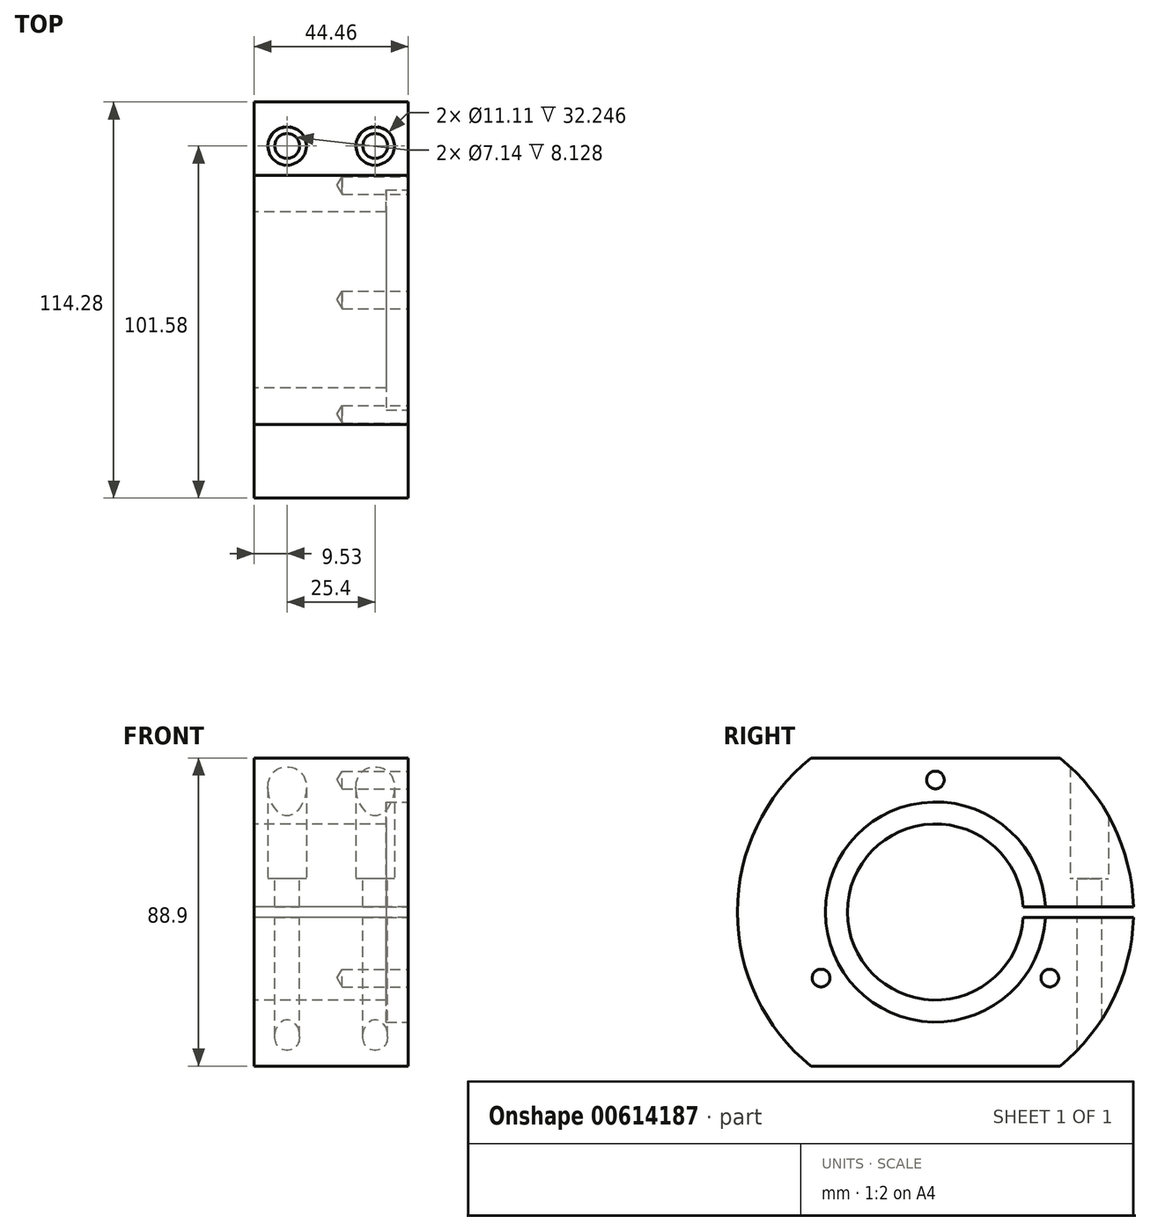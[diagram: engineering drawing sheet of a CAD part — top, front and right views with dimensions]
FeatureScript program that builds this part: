
annotation { "Feature Type Name" : "Feature", "Feature Type Description" : "" }
export const myFeature = defineFeature(function(context is Context, id is Id, definition is map)
    precondition{}
    {
        {
            var Q0;
            Q0=qCreatedBy(makeId("Right.planeOp"),FACE);
            var sketch = newSketch(context, id + "F0", { "sketchPlane" : qUnion([Q0])});
            skCircle(sketch, "E0", {"center": v(0, 0) * mm, "radius": 25.4 * mm});
            skArc(sketch, "E1", {"start": v(-35.92, 44.45) * mm, "mid": v(-57.15, 0) * mm, "end": v(-35.92, -44.45) * mm});
            skLineSegment(sketch, "E2", {"start": v(-95, 0) * mm, "end": v(101.51, 0) * mm, "construction": true});
            skLineSegment(sketch, "E3.0", {"start": v(-35.92, 44.45) * mm, "end": v(35.92, 44.45) * mm});
            skLineSegment(sketch, "E4.MirrorCS", {"start": v(-35.92, -44.45) * mm, "end": v(35.92, -44.45) * mm});
            skArc(sketch, "E5.trimOffspring", {"start": v(35.92, -44.45) * mm, "mid": v(57.15, 0) * mm, "end": v(35.92, 44.45) * mm});
            skPoint(sketch, "E6.orphan", {"position": v(101.51, -44.45) * mm});
            skPoint(sketch, "E7.orphan", {"position": v(-95, -44.45) * mm});
            skPoint(sketch, "E8.orphan", {"position": v(-95, 44.45) * mm});
            skPoint(sketch, "E9.orphan", {"position": v(101.51, 44.45) * mm});
            skSolve(sketch);
        }
        {
            var Q0;
            Q0 = qSketchRegion(id + "F0", true);
            extrude(context, id + "F1", {"entities" : qUnion([Q0]), "endBound" : BoundingType.SYMMETRIC, "depth" : 44.45 * mm, "offsetDistance" : 25.4 * mm});
        }
        {
            var Q0;
            Q0=makeQuery(id+"F1.opExtrude","CAP_FACE",FACE,{"disambiguationData":[OSD([sQuery(id+"F0.wireOp",EDGE,"E0"),sQuery(id+"F0.wireOp",EDGE,"E1"),sQuery(id+"F0.wireOp",EDGE,"E3.0"),sQuery(id+"F0.wireOp",EDGE,"E4.MirrorCS"),sQuery(id+"F0.wireOp",EDGE,"E5.trimOffspring")])],"isStart":false});
            var sketch = newSketch(context, id + "F2", { "sketchPlane" : qUnion([Q0])});
            skCircle(sketch, "E10", {"center": v(0, 0) * mm, "radius": 31.75 * mm});
            skSolve(sketch);
        }
        {
            var Q0;
            Q0 = qSketchRegion(id + "F2", true);
            extrude(context, id + "F3", {"entities" : qUnion([Q0]), "operationType" : NewBodyOperationType.REMOVE, "oppositeDirection" : true, "depth" : 6.35 * mm, "offsetDistance" : 25.4 * mm});
        }
        {
            var Q0;
            Q0=makeQuery(id+"F1.opExtrude","CAP_FACE",FACE,{"disambiguationData":[OSD([sQuery(id+"F0.wireOp",EDGE,"E0"),sQuery(id+"F0.wireOp",EDGE,"E1"),sQuery(id+"F0.wireOp",EDGE,"E3.0"),sQuery(id+"F0.wireOp",EDGE,"E4.MirrorCS"),sQuery(id+"F0.wireOp",EDGE,"E5.trimOffspring")])],"isStart":false});
            var sketch = newSketch(context, id + "F4", { "sketchPlane" : qUnion([Q0])});
            skLineSegment(sketch, "E11", {"start": v(5.07, 0) * mm, "end": v(74.02, 0) * mm});
            skLineSegment(sketch, "E12.0", {"start": v(5.07, -1.52) * mm, "end": v(74.02, -1.52) * mm});
            skLineSegment(sketch, "E13.0", {"start": v(5.07, 1.52) * mm, "end": v(74.02, 1.52) * mm});
            skLineSegment(sketch, "E14", {"start": v(5.07, 1.52) * mm, "end": v(5.07, -1.52) * mm});
            skLineSegment(sketch, "E15", {"start": v(74.02, 1.52) * mm, "end": v(74.02, -1.52) * mm});
            skSolve(sketch);
        }
        {
            var Q0;
            Q0 = qSketchRegion(id + "F4", true);
            extrude(context, id + "F5", {"entities" : qUnion([Q0]), "operationType" : NewBodyOperationType.REMOVE, "endBound" : BoundingType.THROUGH_ALL, "oppositeDirection" : true, "depth" : 25.4 * mm, "offsetDistance" : 25.4 * mm});
        }
        {
            var Q0;
            Q0=qCreatedBy(makeId("Top.planeOp"),FACE);
            cPlane(context, id + "F6", {"entities" : qUnion([Q0]), "cplaneType" : CPlaneType.OFFSET, "offset" : 9.65 * mm, "width" : 152.4 * mm, "height" : 152.4 * mm});
        }
        {
            var Q0;
            Q0=qCreatedBy(id+"F6.planeOp",FACE);
            var sketch = newSketch(context, id + "F7", { "sketchPlane" : qUnion([Q0])});
            skLineSegment(sketch, "E16.0", {"start": v(-22.23, 57.13) * mm, "end": v(22.23, 57.13) * mm, "construction": true});
            skLineSegment(sketch, "E17.0", {"start": v(-22.23, 25.35) * mm, "end": v(22.23, 25.35) * mm, "construction": true});
            skPoint(sketch, "E18.orphan", {"position": v(15.88, 25.35) * mm});
            skLineSegment(sketch, "E19.0", {"start": v(22.23, -35.92) * mm, "end": v(22.23, 35.92) * mm, "construction": true});
            skLineSegment(sketch, "E20.0", {"start": v(-22.23, -35.92) * mm, "end": v(-22.23, 35.92) * mm, "construction": true});
            skLineSegment(sketch, "E21", {"start": v(0, 25.35) * mm, "end": v(0, 57.13) * mm, "construction": true});
            skLineSegment(sketch, "E22.0", {"start": v(12.7, 25.35) * mm, "end": v(12.7, 57.13) * mm, "construction": true});
            skCircle(sketch, "E23", {"center": v(12.7, 44.43) * mm, "radius": 5.56 * mm});
            skCircle(sketch, "E24.MirrorC", {"center": v(-12.7, 44.43) * mm, "radius": 5.56 * mm});
            skSolve(sketch);
        }
        {
            var Q0;
            Q0 = qSketchRegion(id + "F7", true);
            extrude(context, id + "F8", {"entities" : qUnion([Q0]), "operationType" : NewBodyOperationType.REMOVE, "depth" : 50.8 * mm, "offsetDistance" : 25.4 * mm});
        }
        {
            var Q0;
            Q0=makeQuery(id+"F8.boolean.opBoolean","COPY",FACE,{"derivedFrom":makeQuery(id+"F8.opExtrude","CAP_FACE",FACE,{"disambiguationData":[OSD([sQuery(id+"F7.wireOp",EDGE,"E23")])],"isStart":true})});
            var sketch = newSketch(context, id + "F9", { "sketchPlane" : qUnion([Q0])});
            skLineSegment(sketch, "E25.0", {"start": v(0, 25.35) * mm, "end": v(0, 57.13) * mm, "construction": true});
            skPoint(sketch, "E26", {"position": v(12.7, 44.43) * mm});
            skPoint(sketch, "E27.MirrorP", {"position": v(-12.7, 44.43) * mm});
            skSolve(sketch);
        }
        {
            var Q0;
            Q0=sQuery(id+"F9.wireOp",VERTEX,"E27.MirrorP");
            var Q1;
            Q1=sQuery(id+"F9.wireOp",VERTEX,"E26");
            var Q2;
            Q2=makeQuery(id+"F1.opExtrude","SWEPT_BODY",BODY,{"disambiguationData":[OSD([sQuery(id+"F0.wireOp",EDGE,"E0"),sQuery(id+"F0.wireOp",EDGE,"E1"),sQuery(id+"F0.wireOp",EDGE,"E3.0"),sQuery(id+"F0.wireOp",EDGE,"E4.MirrorCS"),sQuery(id+"F0.wireOp",EDGE,"E5.trimOffspring")])]});
            hole(context, id + "F10", {"style" : HoleStyle.SIMPLE, "endStyle" : HoleEndStyle.THROUGH, "holeDiameter" : 7.14 * mm, "majorDiameter" : 6.35 * mm, "isTappedThrough" : true, "tappedDepth" : 25.4 * mm, "tapClearance" : 3, "locations" : qUnion([Q0, Q1]), "scope" : qUnion([Q2])});
        }
        {
            var Q0;
            Q0=makeQuery(id+"F1.opExtrude","CAP_FACE",FACE,{"disambiguationData":[OSD([sQuery(id+"F0.wireOp",EDGE,"E0"),sQuery(id+"F0.wireOp",EDGE,"E1"),sQuery(id+"F0.wireOp",EDGE,"E3.0"),sQuery(id+"F0.wireOp",EDGE,"E4.MirrorCS"),sQuery(id+"F0.wireOp",EDGE,"E5.trimOffspring")])],"isStart":false});
            var sketch = newSketch(context, id + "F11", { "sketchPlane" : qUnion([Q0])});
            skCircle(sketch, "E28", {"center": v(0, 0) * mm, "radius": 38.1 * mm, "construction": true});
            skLineSegment(sketch, "E29", {"start": v(0, 0) * mm, "end": v(0, 96.72) * mm, "construction": true});
            skPoint(sketch, "E30", {"position": v(0, 38.1) * mm});
            skPoint(sketch, "E31.1.0", {"position": v(-33, -19.05) * mm});
            skPoint(sketch, "E31.2.0", {"position": v(33, -19.05) * mm});
            skSolve(sketch);
        }
        {
            var Q0;
            Q0=sQuery(id+"F11.wireOp",VERTEX,"E30");
            var Q1;
            Q1=sQuery(id+"F11.wireOp",VERTEX,"E31.2.0");
            var Q2;
            Q2=sQuery(id+"F11.wireOp",VERTEX,"E31.1.0");
            var Q3;
            Q3=makeQuery(id+"F1.opExtrude","SWEPT_BODY",BODY,{"disambiguationData":[OSD([sQuery(id+"F0.wireOp",EDGE,"E0"),sQuery(id+"F0.wireOp",EDGE,"E1"),sQuery(id+"F0.wireOp",EDGE,"E3.0"),sQuery(id+"F0.wireOp",EDGE,"E4.MirrorCS"),sQuery(id+"F0.wireOp",EDGE,"E5.trimOffspring")])]});
            hole(context, id + "F12", {"style" : HoleStyle.SIMPLE, "endStyle" : HoleEndStyle.BLIND, "standardTappedOrClearance" : lookupTablePath({ "standard" : "ANSI", "engagement" : "75%", "pitch" : "20 tpi", "size" : "1/4", "type" : "Tapped" }), "standardBlindInLast" : lookupTablePath({ "standard" : "ANSI", "engagement" : "75%", "pitch" : "20 tpi", "size" : "1/4", "type" : "Tapped" }), "holeDiameter" : 5.1 * mm, "majorDiameter" : 6.35 * mm, "showTappedDepth" : true, "holeDepth" : 19.05 * mm, "isTappedThrough" : true, "tappedDepth" : 15.24 * mm, "tapClearance" : 3, "locations" : qUnion([Q0, Q1, Q2]), "scope" : qUnion([Q3])});
        }
    });
